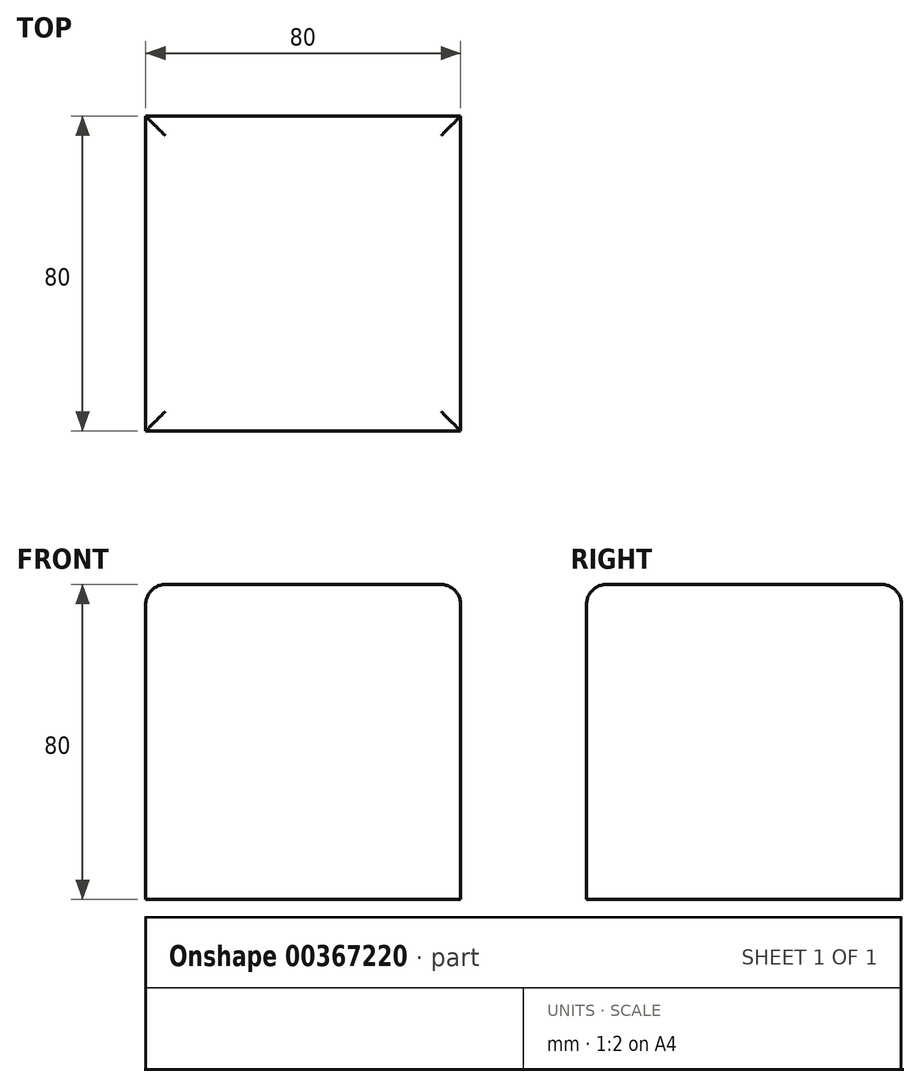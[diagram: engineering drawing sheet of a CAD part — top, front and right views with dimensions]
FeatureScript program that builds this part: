
annotation { "Feature Type Name" : "Feature", "Feature Type Description" : "" }
export const myFeature = defineFeature(function(context is Context, id is Id, definition is map)
    precondition{}
    {
        {
            var Q0;
            Q0=qCreatedBy(makeId("Top.planeOp"),FACE);
            var sketch = newSketch(context, id + "F0", { "sketchPlane" : qUnion([Q0])});
            skLineSegment(sketch, "E0.bottom", {"start": v(-40, 40) * mm, "end": v(40, 40) * mm});
            skLineSegment(sketch, "E0.top", {"start": v(-40, -40) * mm, "end": v(40, -40) * mm});
            skLineSegment(sketch, "E0.left", {"start": v(-40, 40) * mm, "end": v(-40, -40) * mm});
            skLineSegment(sketch, "E0.right", {"start": v(40, 40) * mm, "end": v(40, -40) * mm});
            skPoint(sketch, "E0.middle", {"position": v(0, 0) * mm});
            skSolve(sketch);
        }
        {
            var Q0;
            Q0=makeQuery(id+"F0.imprint","IMPRINT",FACE,{"disambiguationData":[TD([[makeQuery(id+"F0.imprint","IMPRINT",EDGE,{"derivedFrom":sQuery(id+"F0.wireOp",EDGE,"E0.bottom")}),-1.0]])]});
            extrude(context, id + "F1", {"entities" : qUnion([Q0]), "depth" : 80 * mm});
        }
        {
            var Q0;
            Q0=makeQuery(id+"F1.opExtrude","CAP_EDGE",EDGE,{"disambiguationData":[OSD([sQuery(id+"F0.wireOp",EDGE,"E0.bottom")])],"isStart":false});
            var Q1;
            Q1=makeQuery(id+"F1.opExtrude","CAP_EDGE",EDGE,{"disambiguationData":[OSD([sQuery(id+"F0.wireOp",EDGE,"E0.left")])],"isStart":false});
            var Q2;
            Q2=makeQuery(id+"F1.opExtrude","CAP_EDGE",EDGE,{"disambiguationData":[OSD([sQuery(id+"F0.wireOp",EDGE,"E0.right")])],"isStart":false});
            var Q3;
            Q3=makeQuery(id+"F1.opExtrude","CAP_EDGE",EDGE,{"disambiguationData":[OSD([sQuery(id+"F0.wireOp",EDGE,"E0.top")])],"isStart":false});
            fillet(context, id + "F2", {"entities" : qUnion([Q0, Q1, Q2, Q3]), "radius" : 5 * mm, "tangentPropagation" : true, "allowEdgeOverflow" : false});
        }
    });
